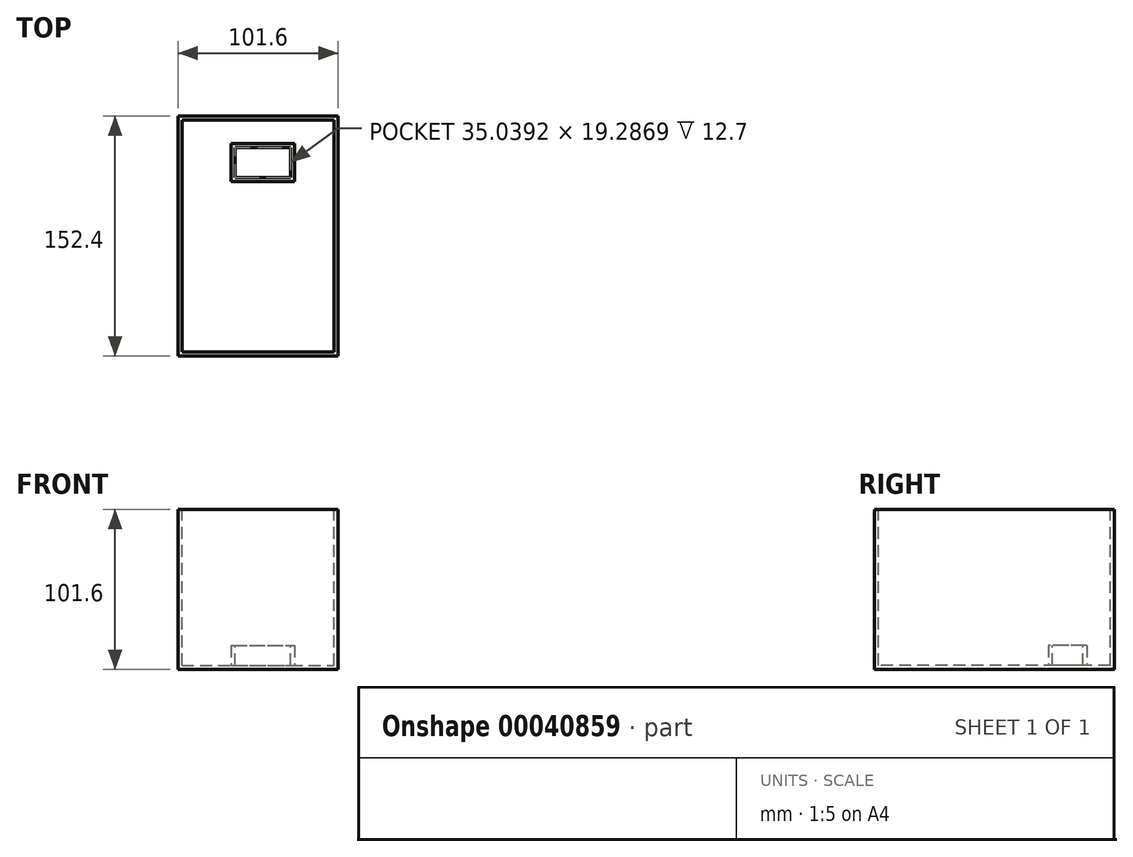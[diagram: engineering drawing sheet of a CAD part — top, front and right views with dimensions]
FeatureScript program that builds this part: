
annotation { "Feature Type Name" : "Feature", "Feature Type Description" : "" }
export const myFeature = defineFeature(function(context is Context, id is Id, definition is map)
    precondition{}
    {
        {
            var Q0;
            Q0=qCreatedBy(makeId("Top.planeOp"),FACE);
            var sketch = newSketch(context, id + "F0", { "sketchPlane" : qUnion([Q0])});
            skLineSegment(sketch, "E0.bottom", {"start": v(-84.03, 78.26) * mm, "end": v(17.57, 78.26) * mm});
            skLineSegment(sketch, "E0.top", {"start": v(-84.03, -74.14) * mm, "end": v(17.57, -74.14) * mm});
            skLineSegment(sketch, "E0.left", {"start": v(-84.03, 78.26) * mm, "end": v(-84.03, -74.14) * mm});
            skLineSegment(sketch, "E0.right", {"start": v(17.57, 78.26) * mm, "end": v(17.57, -74.14) * mm});
            skSolve(sketch);
        }
        {
            var Q0;
            Q0=makeQuery(id+"F0.imprint","IMPRINT",FACE,{"disambiguationData":[TD([[makeQuery(id+"F0.imprint","IMPRINT",EDGE,{"derivedFrom":sQuery(id+"F0.wireOp",EDGE,"E0.bottom")}),-1.0]])]});
            extrude(context, id + "F1", {"entities" : qUnion([Q0]), "depth" : 101.6 * mm});
        }
        {
            var Q0;
            Q0=makeQuery(id+"F1.opExtrude","CAP_FACE",FACE,{"disambiguationData":[OSD([sQuery(id+"F0.wireOp",EDGE,"E0.bottom"),sQuery(id+"F0.wireOp",EDGE,"E0.top"),sQuery(id+"F0.wireOp",EDGE,"E0.left"),sQuery(id+"F0.wireOp",EDGE,"E0.right")])],"isStart":false});
            var sketch = newSketch(context, id + "F2", { "sketchPlane" : qUnion([Q0])});
            skLineSegment(sketch, "E1.bottom", {"start": v(-81.5, 75.72) * mm, "end": v(15.03, 75.72) * mm});
            skLineSegment(sketch, "E1.top", {"start": v(-81.5, -71.6) * mm, "end": v(15.03, -71.6) * mm});
            skLineSegment(sketch, "E1.left", {"start": v(-81.5, 75.72) * mm, "end": v(-81.5, -71.6) * mm});
            skLineSegment(sketch, "E1.right", {"start": v(15.03, 75.72) * mm, "end": v(15.03, -71.6) * mm});
            skSolve(sketch);
        }
        {
            var Q0;
            Q0=makeQuery(id+"F2.imprint","IMPRINT",FACE,{"disambiguationData":[TD([[makeQuery(id+"F2.imprint","IMPRINT",EDGE,{"derivedFrom":sQuery(id+"F2.wireOp",EDGE,"E1.bottom")}),-1.0]])]});
            extrude(context, id + "F3", {"entities" : qUnion([Q0]), "operationType" : NewBodyOperationType.REMOVE, "oppositeDirection" : true, "depth" : 99.06 * mm});
        }
        {
            var Q0;
            Q0=makeQuery(id+"F3.boolean.opBoolean","COPY",FACE,{"derivedFrom":makeQuery(id+"F3.opExtrude","CAP_FACE",FACE,{"disambiguationData":[OSD([sQuery(id+"F2.wireOp",EDGE,"E1.bottom"),sQuery(id+"F2.wireOp",EDGE,"E1.top"),sQuery(id+"F2.wireOp",EDGE,"E1.left"),sQuery(id+"F2.wireOp",EDGE,"E1.right")])],"isStart":false})});
            var sketch = newSketch(context, id + "F4", { "sketchPlane" : qUnion([Q0])});
            skLineSegment(sketch, "E2.bottom", {"start": v(-50.2, 60.88) * mm, "end": v(-10.08, 60.88) * mm});
            skLineSegment(sketch, "E2.top", {"start": v(-50.2, 36.52) * mm, "end": v(-10.08, 36.52) * mm});
            skLineSegment(sketch, "E2.left", {"start": v(-50.2, 60.88) * mm, "end": v(-50.2, 36.52) * mm});
            skLineSegment(sketch, "E2.right", {"start": v(-10.08, 60.88) * mm, "end": v(-10.08, 36.52) * mm});
            skSolve(sketch);
        }
        {
            var Q0;
            Q0=makeQuery(id+"F4.imprint","IMPRINT",FACE,{"disambiguationData":[TD([[makeQuery(id+"F4.imprint","IMPRINT",EDGE,{"derivedFrom":sQuery(id+"F4.wireOp",EDGE,"E2.bottom")}),-1.0]])]});
            extrude(context, id + "F5", {"entities" : qUnion([Q0]), "operationType" : NewBodyOperationType.ADD, "depth" : 12.7 * mm});
        }
        {
            var Q0;
            Q0=makeQuery(id+"F5.opExtrude","CAP_FACE",FACE,{"disambiguationData":[OSD([sQuery(id+"F4.wireOp",EDGE,"E2.bottom"),sQuery(id+"F4.wireOp",EDGE,"E2.top"),sQuery(id+"F4.wireOp",EDGE,"E2.left"),sQuery(id+"F4.wireOp",EDGE,"E2.right")])],"isStart":false});
            var sketch = newSketch(context, id + "F6", { "sketchPlane" : qUnion([Q0])});
            skLineSegment(sketch, "E3.bottom", {"start": v(-47.66, 58.34) * mm, "end": v(-12.62, 58.34) * mm});
            skLineSegment(sketch, "E3.top", {"start": v(-47.66, 39.06) * mm, "end": v(-12.62, 39.06) * mm});
            skLineSegment(sketch, "E3.left", {"start": v(-47.66, 58.34) * mm, "end": v(-47.66, 39.06) * mm});
            skLineSegment(sketch, "E3.right", {"start": v(-12.62, 58.34) * mm, "end": v(-12.62, 39.06) * mm});
            skSolve(sketch);
        }
        {
            var Q0;
            Q0=makeQuery(id+"F6.imprint","IMPRINT",FACE,{"disambiguationData":[TD([[makeQuery(id+"F6.imprint","IMPRINT",EDGE,{"derivedFrom":sQuery(id+"F6.wireOp",EDGE,"E3.bottom")}),-1.0]])]});
            extrude(context, id + "F7", {"entities" : qUnion([Q0]), "operationType" : NewBodyOperationType.REMOVE, "oppositeDirection" : true, "depth" : 12.7 * mm});
        }
    });
